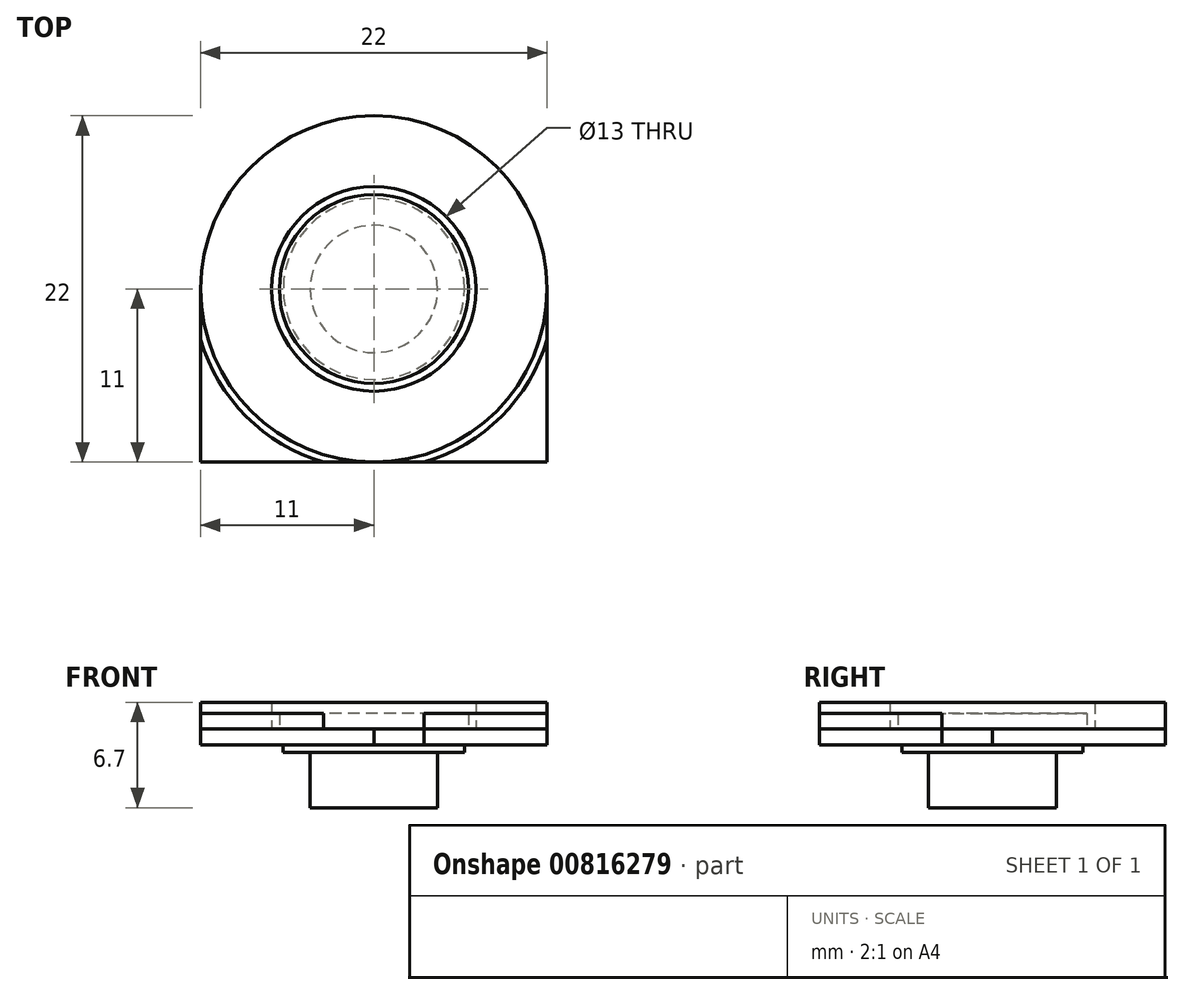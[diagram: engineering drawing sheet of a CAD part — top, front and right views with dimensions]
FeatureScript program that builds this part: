
annotation { "Feature Type Name" : "Feature", "Feature Type Description" : "" }
export const myFeature = defineFeature(function(context is Context, id is Id, definition is map)
    precondition{}
    {
        {
            var Q0;
            Q0=qCreatedBy(makeId("Top.planeOp"),FACE);
            var sketch = newSketch(context, id + "F0", { "sketchPlane" : qUnion([Q0])});
            skCircle(sketch, "E0", {"center": v(0, 0) * mm, "radius": 11 * mm});
            skCircle(sketch, "E1", {"center": v(0, 0) * mm, "radius": 6.5 * mm});
            skCircle(sketch, "E2", {"center": v(0, 0) * mm, "radius": 6 * mm});
            skArc(sketch, "E3", {"start": v(-11, 3.2) * mm, "mid": v(-8.1, 8.1) * mm, "end": v(-3.2, 11) * mm});
            skLineSegment(sketch, "E4", {"start": v(-11, 3.2) * mm, "end": v(-11, 11) * mm});
            skLineSegment(sketch, "E5", {"start": v(-3.2, 11) * mm, "end": v(-11, 11) * mm});
            skLineSegment(sketch, "E6.MirrorCS", {"start": v(-11, -3.2) * mm, "end": v(-11, -11) * mm});
            skLineSegment(sketch, "E7.MirrorCS", {"start": v(-3.2, -11) * mm, "end": v(-11, -11) * mm});
            skArc(sketch, "E8.MirrorCS", {"start": v(-11, -3.2) * mm, "mid": v(-8.1, -8.1) * mm, "end": v(-3.2, -11) * mm});
            skLineSegment(sketch, "E9.MirrorCS", {"start": v(3.2, -11) * mm, "end": v(11, -11) * mm});
            skLineSegment(sketch, "E10.MirrorCS", {"start": v(11, -3.2) * mm, "end": v(11, -11) * mm});
            skArc(sketch, "E11.MirrorCS", {"start": v(11, -3.2) * mm, "mid": v(8.1, -8.1) * mm, "end": v(3.2, -11) * mm});
            skSolve(sketch);
        }
        {
            var Q0;
            Q0=makeQuery(id+"F0.imprint","IMPRINT",FACE,{"disambiguationData":[TD([[makeQuery(id+"F0.imprint","IMPRINT",EDGE,{"derivedFrom":sQuery(id+"F0.wireOp",EDGE,"E0")}),1.0]])]});
            extrude(context, id + "F1", {"entities" : qUnion([Q0]), "depth" : 1.7 * mm, "offsetDistance" : 25 * mm});
        }
        {
            var Q0;
            Q0=makeQuery(id+"F0.imprint","IMPRINT",FACE,{"disambiguationData":[TD([[makeQuery(id+"F0.imprint","IMPRINT",EDGE,{"derivedFrom":sQuery(id+"F0.wireOp",EDGE,"E3")}),1.0]])]});
            var Q1;
            Q1=makeQuery(id+"F0.imprint","IMPRINT",FACE,{"disambiguationData":[TD([[makeQuery(id+"F0.imprint","IMPRINT",EDGE,{"derivedFrom":sQuery(id+"F0.wireOp",EDGE,"E2")}),1.0]])]});
            var Q2;
            Q2=makeQuery(id+"F0.imprint","IMPRINT",FACE,{"disambiguationData":[TD([[makeQuery(id+"F0.imprint","IMPRINT",EDGE,{"derivedFrom":sQuery(id+"F0.wireOp",EDGE,"E6.MirrorCS")}),1.0]])]});
            var Q3;
            Q3=makeQuery(id+"F0.imprint","IMPRINT",FACE,{"disambiguationData":[TD([[makeQuery(id+"F0.imprint","IMPRINT",EDGE,{"derivedFrom":sQuery(id+"F0.wireOp",EDGE,"E9.MirrorCS")}),1.0]])]});
            extrude(context, id + "F2", {"entities" : qUnion([Q0, Q1, Q2, Q3]), "depth" : 1 * mm, "offsetDistance" : 25 * mm});
        }
        {
            var Q0;
            Q0=makeQuery(id+"F0.imprint","IMPRINT",FACE,{"disambiguationData":[TD([[makeQuery(id+"F0.imprint","IMPRINT",EDGE,{"derivedFrom":sQuery(id+"F0.wireOp",EDGE,"E0")}),1.0]])]});
            var sketch = newSketch(context, id + "F3", { "sketchPlane" : qUnion([Q0])});
            skLineSegment(sketch, "E12.0", {"start": v(3.2, -11) * mm, "end": v(11, -11) * mm});
            skLineSegment(sketch, "E13.0", {"start": v(11, -3.2) * mm, "end": v(11, -11) * mm});
            skCircle(sketch, "E14.0", {"center": v(0, 0) * mm, "radius": 11 * mm});
            skLineSegment(sketch, "E15.0", {"start": v(-3.2, -11) * mm, "end": v(-11, -11) * mm});
            skLineSegment(sketch, "E16.0", {"start": v(-11, -3.2) * mm, "end": v(-11, -11) * mm});
            skArc(sketch, "E17.0", {"start": v(-11, 3.2) * mm, "mid": v(-8.1, 8.1) * mm, "end": v(-3.2, 11) * mm});
            skLineSegment(sketch, "E18.0", {"start": v(-11, 3.2) * mm, "end": v(-11, 11) * mm});
            skLineSegment(sketch, "E19", {"start": v(-3.2, 11) * mm, "end": v(0, 11) * mm});
            skLineSegment(sketch, "E20", {"start": v(-11, 3.2) * mm, "end": v(-11, -3.2) * mm});
            skLineSegment(sketch, "E21", {"start": v(-3.2, -11) * mm, "end": v(3.2, -11) * mm});
            skLineSegment(sketch, "E22", {"start": v(11, -3.2) * mm, "end": v(11, 0) * mm});
            skSolve(sketch);
        }
        {
            var Q0;
            Q0=makeQuery(id+"F0.imprint","IMPRINT",FACE,{"disambiguationData":[TD([[makeQuery(id+"F0.imprint","IMPRINT",EDGE,{"derivedFrom":sQuery(id+"F0.wireOp",EDGE,"E3")}),1.0]])]});
            var Q1;
            Q1=makeQuery(id+"F0.imprint","IMPRINT",FACE,{"disambiguationData":[TD([[makeQuery(id+"F0.imprint","IMPRINT",EDGE,{"derivedFrom":sQuery(id+"F0.wireOp",EDGE,"E0")}),1.0]])]});
            var Q2;
            {var subQ4=sQuery(id+"F3.wireOp",EDGE,"E17.0");Q2=makeQuery(id+"F3.imprint","IMPRINT",FACE,{"disambiguationData":[TD([[makeQuery(id+"F3.imprint","IMPRINT",EDGE,{"derivedFrom":subQ4}),-1.0]])]});}
            var Q3;
            {var subQ6=sQuery(id+"F3.wireOp",EDGE,"E15.0");Q3=makeQuery(id+"F3.imprint","IMPRINT",FACE,{"disambiguationData":[TD([[makeQuery(id+"F3.imprint","IMPRINT",EDGE,{"derivedFrom":subQ6}),-1.0]])]});}
            var Q4;
            Q4=makeQuery(id+"F0.imprint","IMPRINT",FACE,{"disambiguationData":[TD([[makeQuery(id+"F0.imprint","IMPRINT",EDGE,{"derivedFrom":sQuery(id+"F0.wireOp",EDGE,"E9.MirrorCS")}),1.0]])]});
            var Q5;
            {var subQ1=sQuery(id+"F3.wireOp",EDGE,"E12.0");Q5=makeQuery(id+"F3.imprint","IMPRINT",FACE,{"disambiguationData":[TD([[makeQuery(id+"F3.imprint","IMPRINT",EDGE,{"derivedFrom":subQ1}),1.0]])]});}
            var Q6;
            Q6=makeQuery(id+"F0.imprint","IMPRINT",FACE,{"disambiguationData":[TD([[makeQuery(id+"F0.imprint","IMPRINT",EDGE,{"derivedFrom":sQuery(id+"F0.wireOp",EDGE,"E2")}),1.0]])]});
            var Q7;
            Q7=makeQuery(id+"F0.imprint","IMPRINT",FACE,{"disambiguationData":[TD([[makeQuery(id+"F0.imprint","IMPRINT",EDGE,{"derivedFrom":sQuery(id+"F0.wireOp",EDGE,"E1")}),1.0]])]});
            extrude(context, id + "F4", {"entities" : qUnion([Q0, Q1, Q2, Q3, Q4, Q5, Q6, Q7]), "oppositeDirection" : true, "depth" : 1 * mm, "offsetDistance" : 25 * mm});
        }
        {
            var Q0;
            Q0=makeQuery(id+"F4.opExtrude","CAP_FACE",FACE,{"disambiguationData":[OSD([sQuery(id+"F0.wireOp",EDGE,"E0")])],"isStart":false});
            var sketch = newSketch(context, id + "F5", { "sketchPlane" : qUnion([Q0])});
            skCircle(sketch, "E23", {"center": v(0, 0) * mm, "radius": 4.05 * mm});
            skCircle(sketch, "E24", {"center": v(0, 0) * mm, "radius": 5.75 * mm});
            skSolve(sketch);
        }
        {
            var Q0;
            Q0 = qSketchRegion(id + "F5", true);
            extrude(context, id + "F6", {"entities" : qUnion([Q0]), "operationType" : NewBodyOperationType.ADD, "depth" : 0.5 * mm, "offsetDistance" : 25 * mm});
        }
        {
            var Q0;
            Q0=makeQuery(id+"F6.boolean.opBoolean","SPLIT",FACE,{"disambiguationData":[TD([makeQuery(id+"F6.opExtrude","SWEPT_FACE",FACE,{"disambiguationData":[OSD([sQuery(id+"F5.wireOp",EDGE,"E23")])]})])],"derivedFrom":makeQuery(id+"F4.opExtrude","CAP_FACE",FACE,{"disambiguationData":[OSD([sQuery(id+"F0.wireOp",EDGE,"E0")])],"isStart":false})});
            extrude(context, id + "F7", {"entities" : qUnion([Q0]), "operationType" : NewBodyOperationType.ADD, "depth" : 4 * mm, "offsetDistance" : 25 * mm});
        }
    });
